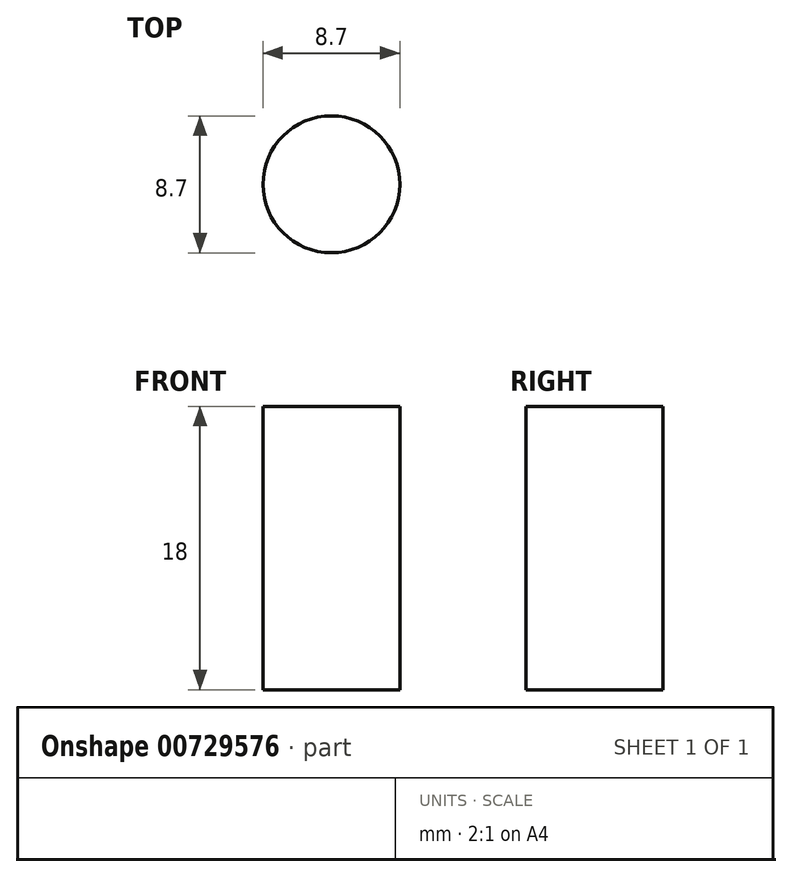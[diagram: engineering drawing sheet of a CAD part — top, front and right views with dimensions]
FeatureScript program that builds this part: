
annotation { "Feature Type Name" : "Feature", "Feature Type Description" : "" }
export const myFeature = defineFeature(function(context is Context, id is Id, definition is map)
    precondition{}
    {
        {
            var Q0;
            Q0=qCreatedBy(makeId("Top.planeOp"),FACE);
            var sketch = newSketch(context, id + "F0", { "sketchPlane" : qUnion([Q0])});
            skCircle(sketch, "E0", {"center": v(0, 0) * mm, "radius": 4.35 * mm});
            skSolve(sketch);
        }
        {
            var Q0;
            Q0 = qSketchRegion(id + "F0", true);
            extrude(context, id + "F1", {"entities" : qUnion([Q0]), "depth" : 18 * mm, "offsetDistance" : 25 * mm});
        }
    });
